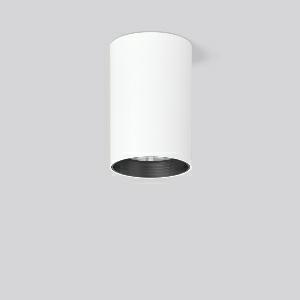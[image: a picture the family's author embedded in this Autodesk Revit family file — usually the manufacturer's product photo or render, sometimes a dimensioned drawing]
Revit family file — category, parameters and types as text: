
# Revit family: heledon_maxi_a_931243_002_9c26
name_source: partatom
category: Lighting Fixtures
units: mm (PartAtom-declared; Revit-internal decimal feet)

## family parameters
Cut with Voids When Loaded = No
Host = Face
Light Source = No
Part Type = Normal
Room Calculation Point = No
Round Connector Dimension = Use Diameter
Shared = No

## types (1)
- HELEDON maxi A (1 x LED Modul 920 meat+, 1900 lm, 2000)
    Apparent Load = 33 VA
    Approval mark = CE
    CIE Flux Codes = 96 99 100 100 100
    Color Rendering = 90
    Color Temperature = 2000
    Default Elevation = 1800 mm
    Description = Series: HELEDON maxi
Cylindrical surface-mounted downlight. Housing: die-cast aluminium, powder-coated. Internal ceiling frame polycarbonate with bayonet mounting. Black plastic ring and recessed LED to prevent glare from the side. Optical assembly with lens made of plastic (polycarbonate) for the best homogeneous light distribution - can be changed without tools. Special LED for illumination of meat included. Suitable for Ceiling mounting. Easy installation with a separate ceiling frame with bayonet mounting and plug connection. Driver integrated. Connected via plug-in connector. High quality converter without flickering and stroboscopic effect. The following accessories can be mounted without use of tools: interchangeable lenses, decorative glasses, honeycomb louvre, clear and frosted diffusers, white interchangeable plastic ring. 
Colour: traffic white, matt (RAL 9016)
Diameter: 123 mm
Height: 183 mm
Lamp: LED
Socket: without socket
Colour temperature: meat +
System power: 33 W
Rated luminous flux: 1900 lm
Luminous efficiency: 58 lm/W
Control gear: Regulated power supply
Protection class: I
Type of protection: IP 20
    Height = 183 mm
    Lamp = 1 x LED Modul 920 meat+
    Lamp Light Flux = 1900 lm
    Lamp count = 1
    Length = 123 mm
    Lifetime = 50000 h
    Luminous efficacy = 58 lm/W
    Manufacturer = RZB
    ModVariant = No
    Model = 931243.002
    Mounting Place = Ceiling
    Mounting Type = Surface mounted
    Number of Poles = 1
    OnlyDefault = Yes
    Power Factor = 1
    Product Name = HELEDON maxi A
    Product group = Surface mounted downlights
    ProductGroupID = 302
    Protection Class = Protection class I
    Protection Degree = IP 20
    RLX_Detail_Level = 1
    RLX_Emergency_Light_Flux = 0 lm
    RLX_Emergency_Type = 0
    RLX_Emergency_Type_DB = No
    RlxData = <blob elided: 98585 chars, md5=4166e7e3>
    Socket = socket
    Standby Power = 0 W
    System Light Flux = 1900 lm
    System Power = 33 W
    Type Comments = Product without accessories
    Type Image = 931193.002.jpg
    URL = http://relux.com
    VarID = ---
    Voltage = 230 V
    Voltage Range = 220-240 V
    Weight = 0.00 kg
    Width = 0 mm  [stored 0 ft]

note: [stored X ft] marks values corroborated as IEEE doubles in the binary element streams (Revit-internal decimal feet)

## geometry (parser evidence)
native form markers: Blend x4, Sweep x12
no freeform markers — native parametric forms only
